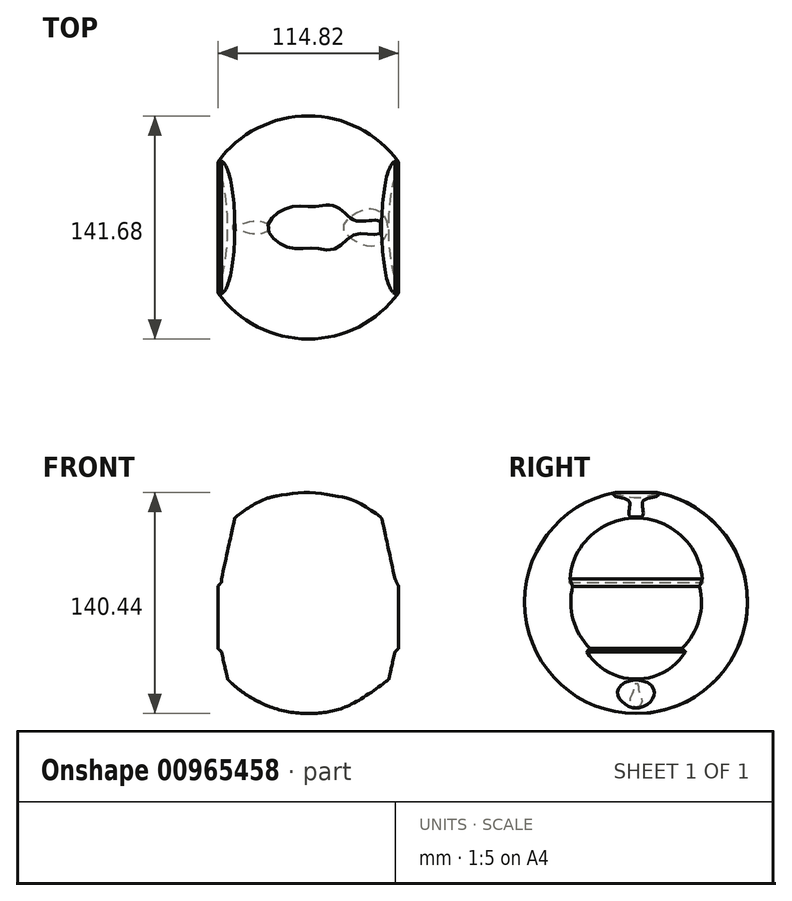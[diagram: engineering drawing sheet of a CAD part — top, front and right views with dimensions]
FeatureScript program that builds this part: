
annotation { "Feature Type Name" : "Feature", "Feature Type Description" : "" }
export const myFeature = defineFeature(function(context is Context, id is Id, definition is map)
    precondition{}
    {
        {
            var Q0;
            Q0=qCreatedBy(makeId("Right.planeOp"),FACE);
            var sketch = newSketch(context, id + "F0", { "sketchPlane" : qUnion([Q0])});
            skArc(sketch, "E0", {"start": v(0, -70.84) * mm, "mid": v(70.84, 0) * mm, "end": v(0, 70.84) * mm});
            skLineSegment(sketch, "E1", {"start": v(0, 70.84) * mm, "end": v(0, -70.84) * mm});
            skSolve(sketch);
        }
        {
            var Q0;
            Q0=makeQuery(id+"F0.imprint","IMPRINT",FACE,{"disambiguationData":[TD([[makeQuery(id+"F0.imprint","IMPRINT",EDGE,{"derivedFrom":sQuery(id+"F0.wireOp",EDGE,"E0")}),1.0]])]});
            var Q1;
            Q1=sQuery(id+"F0.wireOp",EDGE,"E1");
            revolve(context, id + "F1", {"surfaceOperationType" : NewSurfaceOperationType.NEW, "entities" : qUnion([Q0]), "axis" : qUnion([Q1]), "revolveType" : RevolveType.FULL});
        }
        {
            var Q0;
            Q0=qCreatedBy(makeId("Front.planeOp"),FACE);
            var sketch = newSketch(context, id + "F2", { "sketchPlane" : qUnion([Q0])});
            skFitSpline(sketch, "E2", {"points": [v(-46.66, 53.26) * mm, v(-42.68, 57.1) * mm, v(-36.18, 61.75) * mm, v(-27.03, 65.6) * mm, v(-18.27, 67.72) * mm, v(-6.87, 69.18) * mm, v(4.54, 69.44) * mm, v(16.87, 67.45) * mm, v(27.09, 65.2) * mm, v(38.63, 59.23) * mm, v(45.79, 53.92) * mm], "startDerivative": vector(49.78, 50.8) * mm, "endDerivative": vector(68.98, -54.75) * mm});
            skLineSegment(sketch, "E3", {"start": v(-46.66, 53.26) * mm, "end": v(-55.1, 14.76) * mm});
            skLineSegment(sketch, "E4", {"start": v(-55.1, 14.76) * mm, "end": v(-55.1, 12.6) * mm});
            skLineSegment(sketch, "E5", {"start": v(-55.1, 12.6) * mm, "end": v(-57.4, 10) * mm});
            skLineSegment(sketch, "E6", {"start": v(-57.4, 10) * mm, "end": v(-57.4, -29.43) * mm});
            skLineSegment(sketch, "E7", {"start": v(-57.4, -29.43) * mm, "end": v(-55.1, -31.6) * mm});
            skLineSegment(sketch, "E8", {"start": v(-55.1, -31.6) * mm, "end": v(-51.14, -49.17) * mm});
            skLineSegment(sketch, "E9", {"start": v(0, 45.33) * mm, "end": v(0, -7.68) * mm});
            skLineSegment(sketch, "E10.MirrorCS", {"start": v(46.66, 53.26) * mm, "end": v(55.1, 14.76) * mm});
            skLineSegment(sketch, "E11.MirrorCS", {"start": v(57.4, 10) * mm, "end": v(57.4, -29.43) * mm});
            skLineSegment(sketch, "E12", {"start": v(45.79, 53.92) * mm, "end": v(46.66, 53.26) * mm});
            skLineSegment(sketch, "E13", {"start": v(55.1, 14.76) * mm, "end": v(57.4, 10) * mm});
            skLineSegment(sketch, "E14.MirrorCS", {"start": v(57.4, -29.43) * mm, "end": v(55.1, -31.6) * mm});
            skLineSegment(sketch, "E15.MirrorCS", {"start": v(55.1, -31.6) * mm, "end": v(51.14, -49.17) * mm});
            skFitSpline(sketch, "E16", {"points": [v(-51.14, -49.17) * mm, v(-40.49, -58.08) * mm, v(-19.04, -68.38) * mm, v(4.07, -71.17) * mm, v(26.07, -65.6) * mm, v(51.14, -49.17) * mm], "startDerivative": vector(59.77, -56.32) * mm, "endDerivative": vector(108.38, 80.91) * mm});
            skSolve(sketch);
        }
        {
            var Q0;
            Q0 = qSketchRegion(id + "F2", true);
            extrude(context, id + "F3", {"entities" : qUnion([Q0]), "operationType" : NewBodyOperationType.INTERSECT, "endBound" : BoundingType.SYMMETRIC, "depth" : 176.28 * mm, "offsetDistance" : 25.4 * mm});
        }
    });
